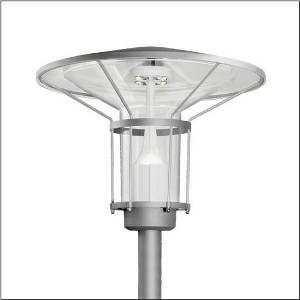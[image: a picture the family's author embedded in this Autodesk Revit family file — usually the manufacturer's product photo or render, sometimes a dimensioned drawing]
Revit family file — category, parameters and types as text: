
# Revit family: laterne_classic_iq___pl1_2s_5xa5245rf14h_f81d
name_source: partatom
category: Lighting Fixtures
units: mm (PartAtom-declared; Revit-internal decimal feet)

## family parameters
Cut with Voids When Loaded = No
Host = Face
Light Source = No
Part Type = Normal
Room Calculation Point = No
Round Connector Dimension = Use Diameter
Shared = No

## types (1)
- --- (1 x LED, 2670 lm, 18.5 W, 4000K)
    Apparent Load = 19 VA
    CIE Flux Codes = 21 60 93 97 100
    Color Rendering = 70
    Color Temperature = 4000K
    Default Elevation = 1800 mm
    Description = Lantern Classic iQ, mast luminaire, Module 540 iQ-SR, primary light control with 3 zone facetted reflector, of plastic, silver coated, highly specular, structured, primary optical cover: cover, of PMMA, transparent, light distribution: PL1.2s, light emission: direct distribution, primary light characteristic: symmetric, installation type: post-top, LED, High Power LED, rated luminous flux: 2.670lm, luminous efficacy: 144lm/W, light colour: 740, colour temperature: 4000K, control gear: iQ Street-Remote, control: pre-setting: logarithmic dimming characteristic, Street-Remote, Auto-Match, Temp-Guard, Lumen-Switch, Night-Set, Smart-Wire, Light-Fading, Desk-Remote (wireless, voltage-free reading and setting of iQ features in the workshop via application-optimized NFC function/RFID function), optimised constant luminous flux control (CLO 2.0), with terminal, 6-pole, max. 2.5mm², mains connection: 230..240V, AC, 50/60Hz, start of lifetime: 19W, end of service life: 20W, reduction: 9W, luminaire housing, upper part, of glass-fibre reinforced polyester, coated, Siteco® metallic grey (DB 702S), diameter: 750mm, height: 596mm, spigot size: d x l = 76 x 70mm (post-top) | with reducer (optional accessory) 60 x 70mm, mounting height: 3..5m, post-top mast mounting element, of diecast aluminium, coated, Siteco® metallic grey (DB 702S), Module 540 iQ-SR, traffic white (RAL 9016), equipment: standard, protection rating (complete): IP65, insulation class (complete): insulation class II (safety insulation), certification: CE, ENEC, VDE, packaging unit: 1 piece

Light Distribution: PL1.2s
    Height = 596 mm
    Lamp = 1 x LED
    Lamp Light Flux = 2670 lm
    Lamp Power = 18.5 W
    Lamp count = 1
    Length = 750 mm
    Luminous efficacy = 144 lm/W
    Manufacturer = Siteco
    ModVariant = No
    Model = 5XA5245RF14H
    Number of Poles = 1
    OnlyDefault = Yes
    Power Factor = 1
    Product Name = Laterne Classic iQ | PL1.2s
    Product group = mast luminaire | pylon top
    ProductGroupID = 6100
    Protection Class = Protection class II
    Protection Degree = IP 65
    RLX_Detail_Level = 1
    RLX_Emergency_Light_Flux = 0 lm
    RLX_Emergency_Type = 0
    RLX_Emergency_Type_DB = No
    RlxData = <blob elided: 37869 chars, md5=52ed2e5e>
    Socket = socket
    Standby Power = 0 W
    System Light Flux = 2670 lm
    System Power = 19 W
    Type Comments = factory setting: luminous flux: 100 % | dim-lin: 254 | 385 mA
    Type Image = l_1006052.jpg
    URL = http://relux.com
    VarID = @adj_145704
    Voltage = 0 V
    Weight = 0.00 kg
    Width = 0 mm  [stored 0 ft]

note: [stored X ft] marks values corroborated as IEEE doubles in the binary element streams (Revit-internal decimal feet)

## geometry (parser evidence)
native form markers: Blend x4, Sweep x12
no freeform markers — native parametric forms only
